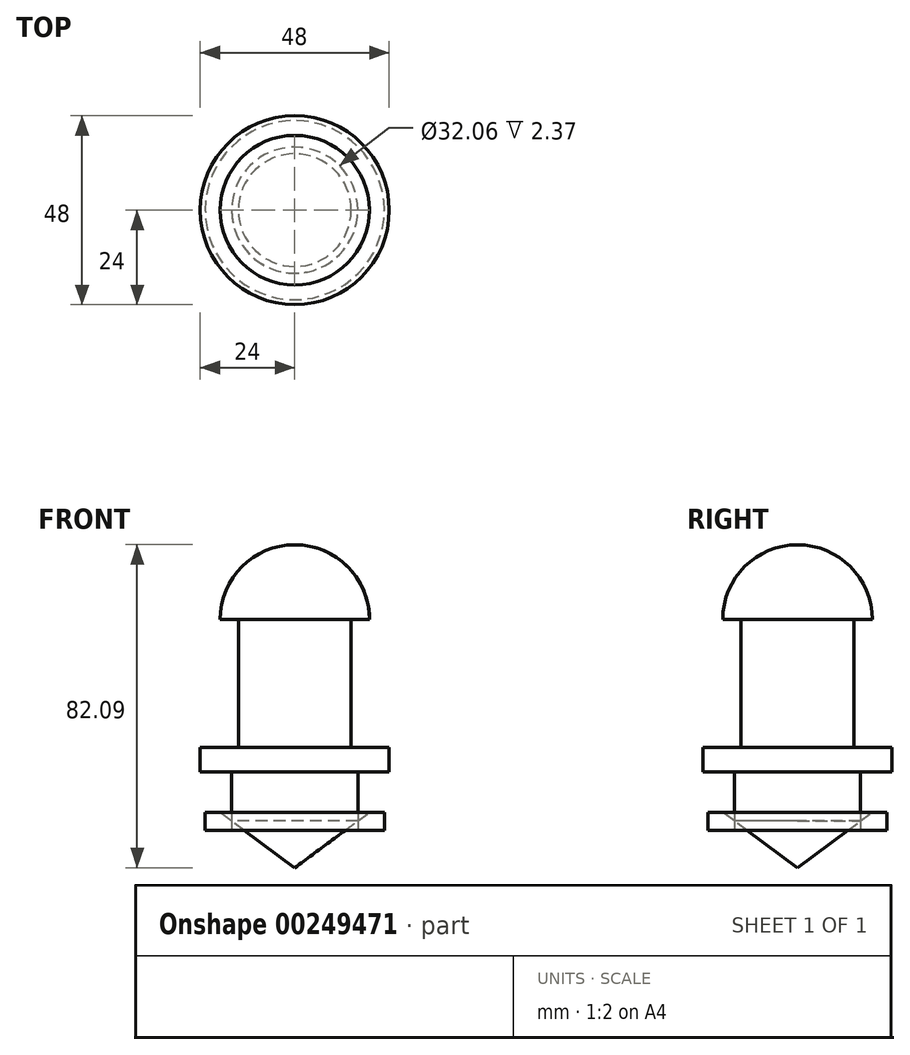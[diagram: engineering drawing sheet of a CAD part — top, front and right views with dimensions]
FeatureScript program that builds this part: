
annotation { "Feature Type Name" : "Feature", "Feature Type Description" : "" }
export const myFeature = defineFeature(function(context is Context, id is Id, definition is map)
    precondition{}
    {
        {
            var Q0;
            Q0=qCreatedBy(makeId("Front.planeOp"),FACE);
            var sketch = newSketch(context, id + "F0", { "sketchPlane" : qUnion([Q0])});
            skLineSegment(sketch, "E0.bottom", {"start": v(0, -9.53) * mm, "end": v(18.98, -21.77) * mm});
            skLineSegment(sketch, "E0.left", {"start": v(0, -9.53) * mm, "end": v(0, 72.56) * mm});
            skLineSegment(sketch, "E0.right", {"start": v(18.98, -21.77) * mm, "end": v(18.98, 53.58) * mm, "construction": true});
            skLineSegment(sketch, "E1", {"start": v(18.98, 53.58) * mm, "end": v(14.34, 53.58) * mm});
            skLineSegment(sketch, "E2", {"start": v(14.34, 53.58) * mm, "end": v(14.34, 21.05) * mm});
            skLineSegment(sketch, "E3", {"start": v(14.34, 21.05) * mm, "end": v(24, 21.05) * mm});
            skLineSegment(sketch, "E4", {"start": v(24, 21.05) * mm, "end": v(24, 14.89) * mm});
            skLineSegment(sketch, "E5", {"start": v(24, 14.89) * mm, "end": v(16.03, 14.89) * mm});
            skLineSegment(sketch, "E6", {"start": v(16.03, 14.89) * mm, "end": v(16.03, 0) * mm});
            skLineSegment(sketch, "E7", {"start": v(22.74, 0) * mm, "end": v(16.03, 0) * mm});
            skLineSegment(sketch, "E8", {"start": v(22.74, 4.56) * mm, "end": v(22.74, 0) * mm});
            skLineSegment(sketch, "E9", {"start": v(18.98, 4.56) * mm, "end": v(22.74, 4.56) * mm});
            skLineSegment(sketch, "E10", {"start": v(18.98, 4.56) * mm, "end": v(0, -9.53) * mm});
            skArc(sketch, "E11", {"start": v(18.98, 53.58) * mm, "mid": v(13.42, 67) * mm, "end": v(0, 72.56) * mm});
            skSolve(sketch);
        }
        {
            var Q0;
            Q0 = qSketchRegion(id + "F0", true);
            var Q1;
            Q1=sQuery(id+"F0.wireOp",EDGE,"E0.left");
            revolve(context, id + "F1", {"entities" : qUnion([Q0]), "axis" : qUnion([Q1]), "revolveType" : RevolveType.FULL});
        }
    });
